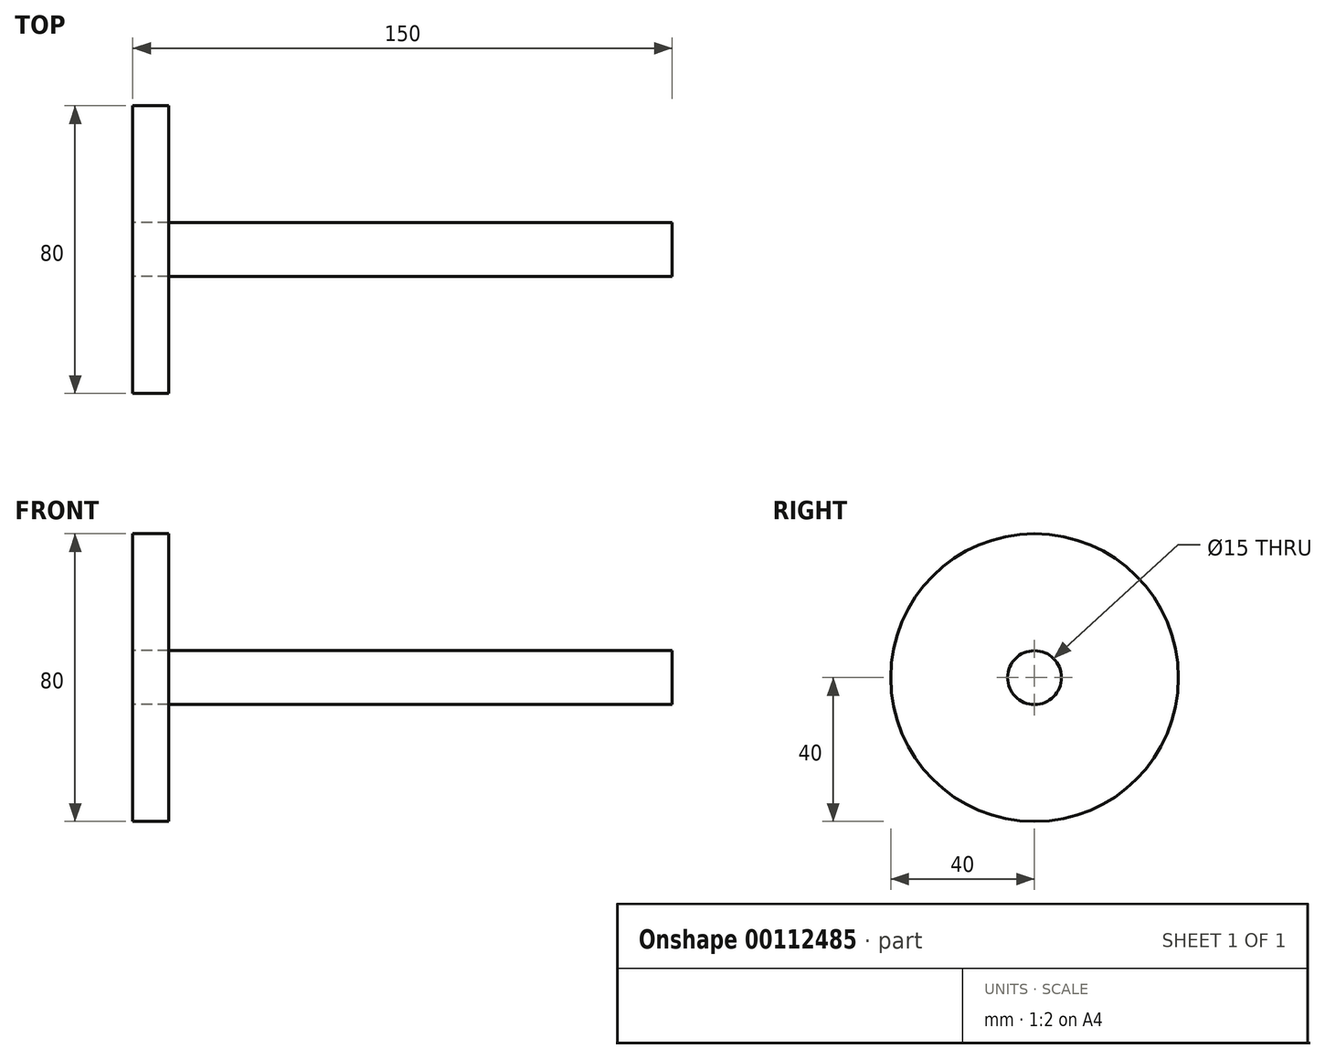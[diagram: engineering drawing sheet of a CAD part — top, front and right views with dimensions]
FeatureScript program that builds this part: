
annotation { "Feature Type Name" : "Feature", "Feature Type Description" : "" }
export const myFeature = defineFeature(function(context is Context, id is Id, definition is map)
    precondition{}
    {
        {
            var Q0;
            Q0=qCreatedBy(makeId("Front.planeOp"),FACE);
            var sketch = newSketch(context, id + "F0", { "sketchPlane" : qUnion([Q0])});
            skLineSegment(sketch, "E0.bottom", {"start": v(-5, 40) * mm, "end": v(5, 40) * mm});
            skLineSegment(sketch, "E0.left", {"start": v(-5, 40) * mm, "end": v(-5, 0) * mm});
            skLineSegment(sketch, "E0.right", {"start": v(5, 40) * mm, "end": v(5, 0) * mm});
            skLineSegment(sketch, "E1.bottom", {"start": v(-5, 7.5) * mm, "end": v(145, 7.5) * mm});
            skLineSegment(sketch, "E1.left", {"start": v(-5, 7.5) * mm, "end": v(-5, 0) * mm});
            skLineSegment(sketch, "E1.right", {"start": v(145, 7.5) * mm, "end": v(145, 0) * mm});
            skLineSegment(sketch, "E2", {"start": v(-74.5, 0) * mm, "end": v(233.3, 0) * mm});
            skSolve(sketch);
        }
        {
            var Q0;
            {var subQ0=sQuery(id+"F0.wireOp",EDGE,"E0.bottom");Q0=makeQuery(id+"F0.imprint","IMPRINT",FACE,{"disambiguationData":[TD([[makeQuery(id+"F0.imprint","IMPRINT",EDGE,{"derivedFrom":subQ0}),-1.0]])]});}
            var Q1;
            {var subQ5=sQuery(id+"F0.wireOp",EDGE,"E1.right");Q1=makeQuery(id+"F0.imprint","IMPRINT",FACE,{"disambiguationData":[TD([[makeQuery(id+"F0.imprint","IMPRINT",EDGE,{"derivedFrom":subQ5}),-1.0]])]});}
            var Q2;
            Q2=sQuery(id+"F0.wireOp",EDGE,"E2");
            revolve(context, id + "F1", {"entities" : qUnion([Q0, Q1]), "axis" : qUnion([Q2]), "revolveType" : RevolveType.FULL});
        }
    });
